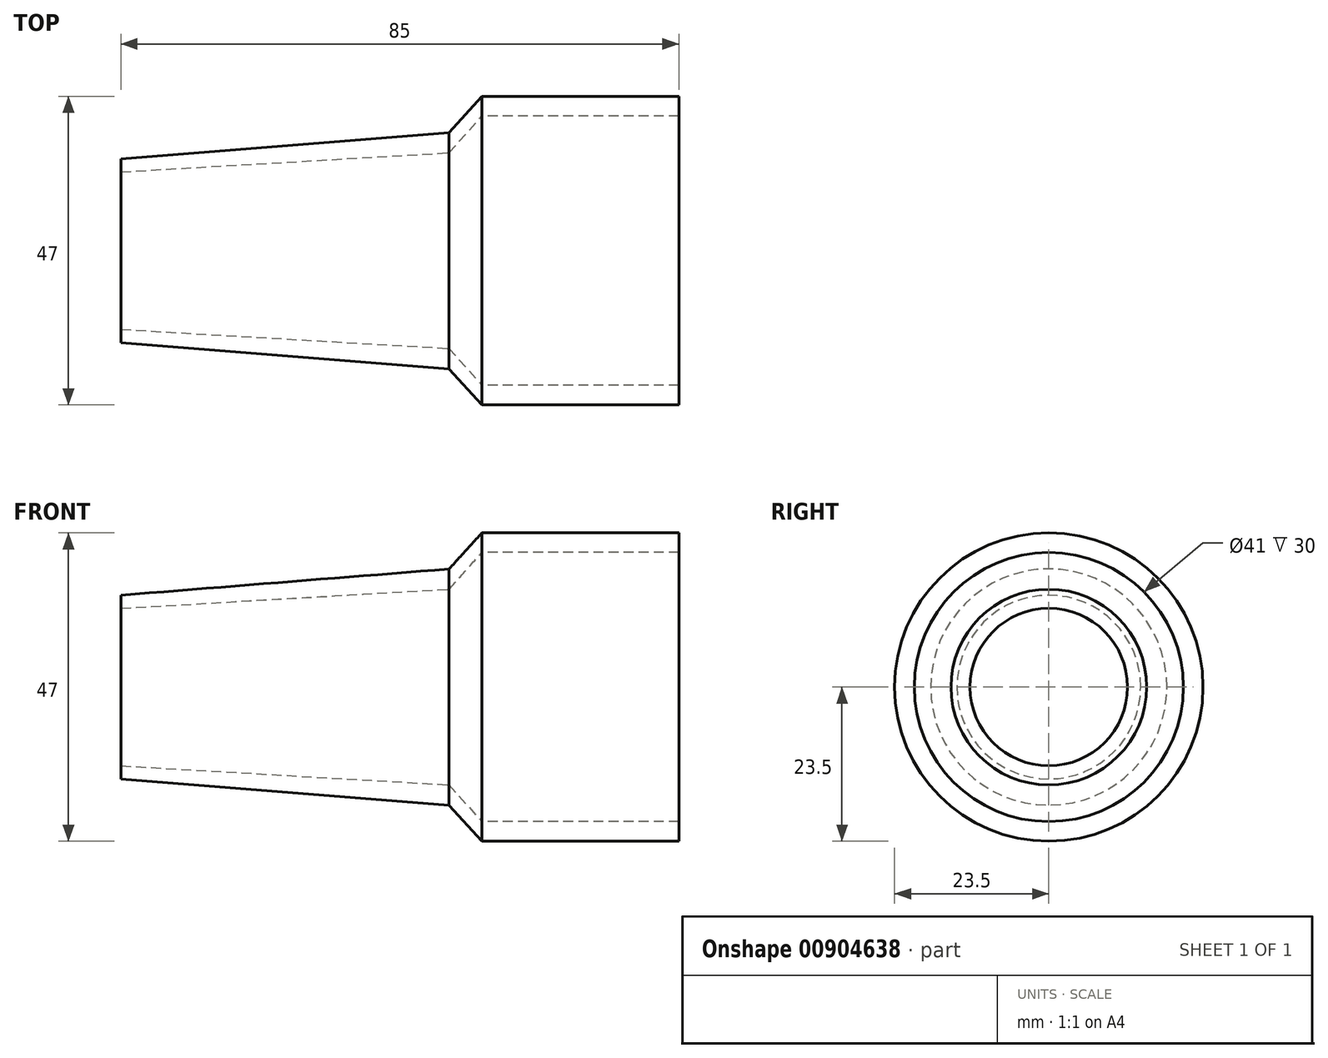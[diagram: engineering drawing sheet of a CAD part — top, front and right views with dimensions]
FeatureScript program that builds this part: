
annotation { "Feature Type Name" : "Feature", "Feature Type Description" : "" }
export const myFeature = defineFeature(function(context is Context, id is Id, definition is map)
    precondition{}
    {
        {
            var Q0;
            Q0=qCreatedBy(makeId("Top.planeOp"),FACE);
            var sketch = newSketch(context, id + "F0", { "sketchPlane" : qUnion([Q0])});
            skLineSegment(sketch, "E0", {"start": v(0, 20.5) * mm, "end": v(30, 20.5) * mm});
            skLineSegment(sketch, "E1", {"start": v(30, 20.5) * mm, "end": v(30, 23.5) * mm});
            skLineSegment(sketch, "E2", {"start": v(30, 23.5) * mm, "end": v(0, 23.5) * mm});
            skLineSegment(sketch, "E3", {"start": v(0, 23.5) * mm, "end": v(-5, 18) * mm});
            skLineSegment(sketch, "E4", {"start": v(-5, 18) * mm, "end": v(-55, 14) * mm});
            skLineSegment(sketch, "E5", {"start": v(-55, 14) * mm, "end": v(-55, 12) * mm});
            skLineSegment(sketch, "E6", {"start": v(-55, 12) * mm, "end": v(-5, 14.9) * mm});
            skLineSegment(sketch, "E7", {"start": v(-5, 14.9) * mm, "end": v(0, 20.5) * mm});
            skLineSegment(sketch, "E8", {"start": v(-73.34, 0) * mm, "end": v(60.24, 0) * mm});
            skSolve(sketch);
        }
        {
            var Q0;
            Q0=makeQuery(id+"F0.imprint","IMPRINT",FACE,{"disambiguationData":[TD([[makeQuery(id+"F0.imprint","IMPRINT",EDGE,{"derivedFrom":sQuery(id+"F0.wireOp",EDGE,"E0")}),1.0]])]});
            var Q1;
            Q1=sQuery(id+"F0.wireOp",EDGE,"E8");
            revolve(context, id + "F1", {"surfaceOperationType" : NewSurfaceOperationType.NEW, "entities" : qUnion([Q0]), "axis" : qUnion([Q1]), "revolveType" : RevolveType.FULL});
        }
    });
